# Revit family: Ascoli Four Bar Family
name_source: partatom
category: Lighting Fixtures
revit_build: Autodesk Revit 2018 (Build: 20170223_1515(x64)
units: mm (PartAtom-declared; Revit-internal decimal feet)

## family parameters
Always vertical = Yes
Cut with Voids When Loaded = No
Host = Ceiling
Light Source = No
OmniClass Number = 23.80.70.11
OmniClass Title = Luminaries for Internal Lighting
Part Type = Normal
Room Calculation Point = No
Round Connector Dimension = Use Diameter
Shared = No

## types (4) — shared parameters
Dimmable = Lamp Dependant
Efficacy (lm/w) = Lamp Dependant
Electrical Class = Class 2
IP Rating = IP20
Lamp = 4 X 50W Max
Light Source Fixed = No
Main Material = Aluminium
Power (Watts) = 50W max
Product Location = Ceiling

## per-type parameters (varying)
| type | Main Finish | Product SKU |
| Ascoli Four Bar - White | Textured White | 1286007 |
| Ascoli Four Bar - Bronze | Bronze | 1286008 |
| Ascoli Four Bar - Matt Nickel | Matt Nickel | 1286014 |
| Ascoli Four Bar - Matt Black | Matt Smooth Black | 1286084 |

note: column(s) folded — value = type name in every type: Product Name

## geometry (parser evidence)
native form markers: Sweep x2
no freeform markers — native parametric forms only
